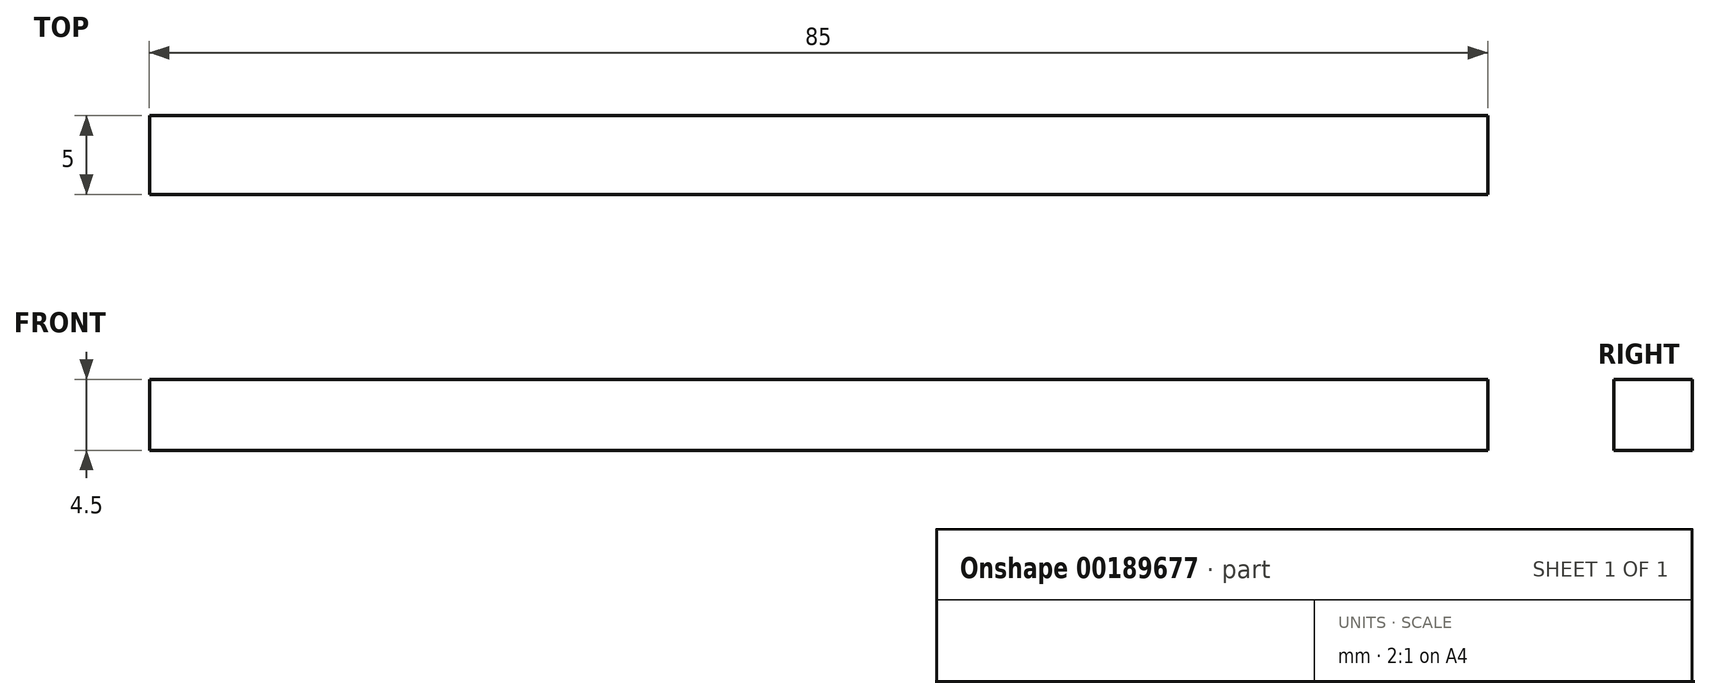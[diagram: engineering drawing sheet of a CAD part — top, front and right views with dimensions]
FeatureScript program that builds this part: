
annotation { "Feature Type Name" : "Feature", "Feature Type Description" : "" }
export const myFeature = defineFeature(function(context is Context, id is Id, definition is map)
    precondition{}
    {
        {
            var Q0;
            Q0=qCreatedBy(makeId("Top.planeOp"),FACE);
            var sketch = newSketch(context, id + "F0", { "sketchPlane" : qUnion([Q0])});
            skLineSegment(sketch, "E0.bottom", {"start": v(-3.29, 0.42) * mm, "end": v(81.71, 0.42) * mm});
            skLineSegment(sketch, "E0.top", {"start": v(-3.29, -4.58) * mm, "end": v(81.71, -4.58) * mm});
            skLineSegment(sketch, "E0.left", {"start": v(-3.29, 0.42) * mm, "end": v(-3.29, -4.58) * mm});
            skLineSegment(sketch, "E0.right", {"start": v(81.71, 0.42) * mm, "end": v(81.71, -4.58) * mm});
            skSolve(sketch);
        }
        {
            var Q0;
            Q0=makeQuery(id+"F0.imprint","IMPRINT",FACE,{"disambiguationData":[TD([[makeQuery(id+"F0.imprint","IMPRINT",EDGE,{"derivedFrom":sQuery(id+"F0.wireOp",EDGE,"E0.bottom")}),-1.0]])]});
            extrude(context, id + "F1", {"entities" : qUnion([Q0]), "depth" : 4.5 * mm, "offsetDistance" : 25 * mm});
        }
    });
